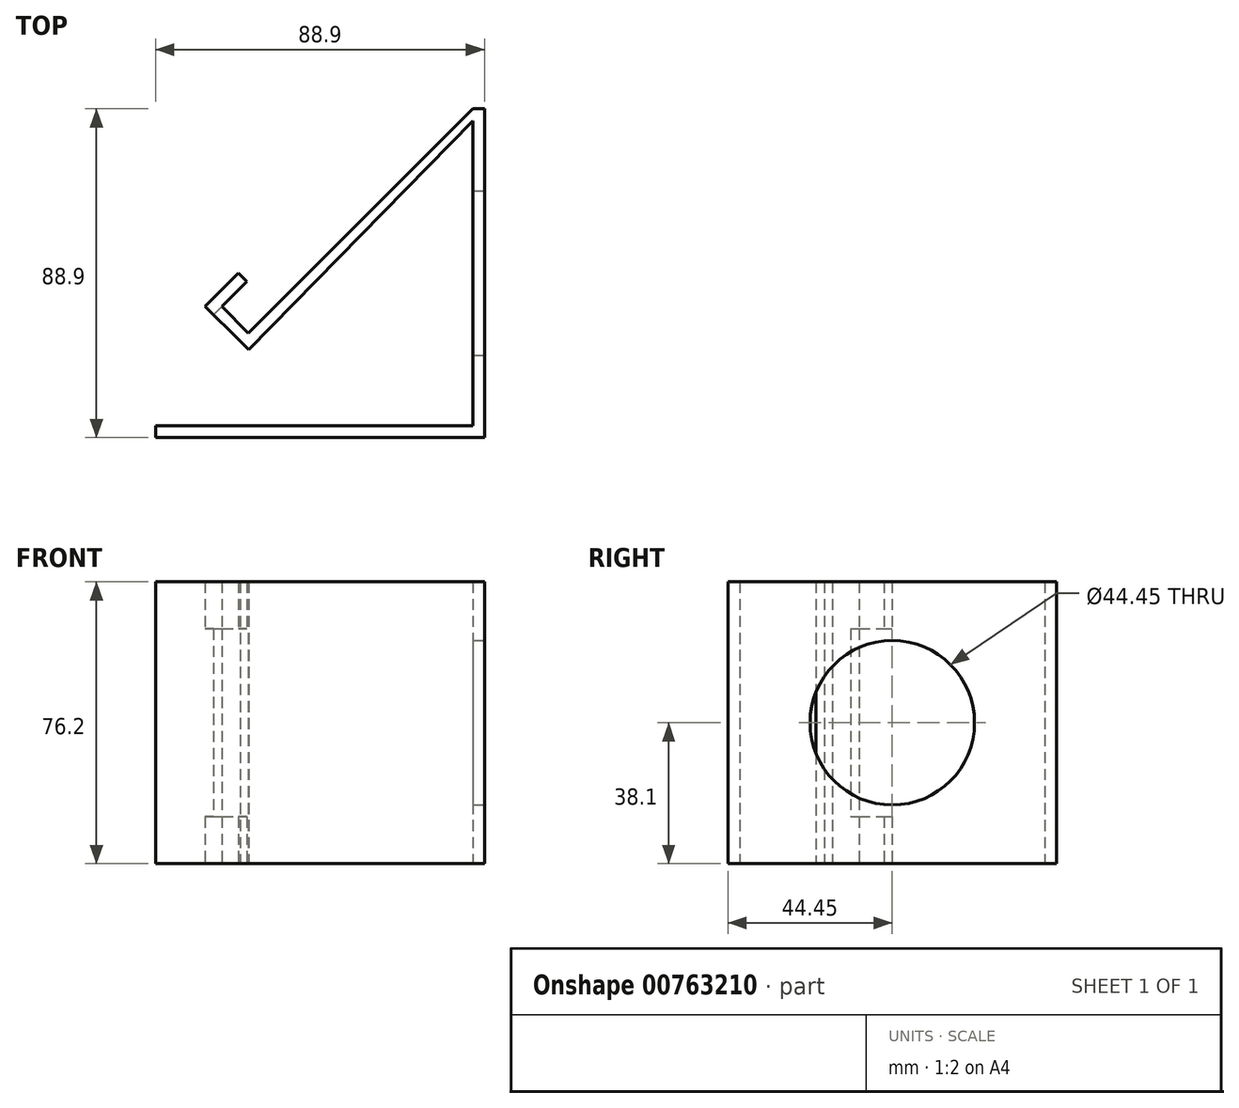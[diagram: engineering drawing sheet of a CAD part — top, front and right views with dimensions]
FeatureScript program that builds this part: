
annotation { "Feature Type Name" : "Feature", "Feature Type Description" : "" }
export const myFeature = defineFeature(function(context is Context, id is Id, definition is map)
    precondition{}
    {
        {
            var Q0;
            Q0=qCreatedBy(makeId("Top.planeOp"),FACE);
            var sketch = newSketch(context, id + "F0", { "sketchPlane" : qUnion([Q0])});
            skLineSegment(sketch, "E0.bottom", {"start": v(25.2, 38.37) * mm, "end": v(50.6, 38.37) * mm});
            skLineSegment(sketch, "E0.top", {"start": v(25.2, -8.48) * mm, "end": v(50.6, -8.48) * mm});
            skLineSegment(sketch, "E0.left", {"start": v(25.2, 38.37) * mm, "end": v(25.2, -8.48) * mm});
            skLineSegment(sketch, "E0.right", {"start": v(50.6, 38.37) * mm, "end": v(50.6, -8.48) * mm});
            skLineSegment(sketch, "E1", {"start": v(50.6, 38.37) * mm, "end": v(25.2, 65.41) * mm});
            skLineSegment(sketch, "E2", {"start": v(25.2, 65.41) * mm, "end": v(25.2, 38.37) * mm});
            skLineSegment(sketch, "E3", {"start": v(25.2, 65.41) * mm, "end": v(-24.23, -8.48) * mm});
            skLineSegment(sketch, "E4", {"start": v(-24.23, -8.48) * mm, "end": v(-19.15, -8.48) * mm});
            skLineSegment(sketch, "E5", {"start": v(-19.15, -8.48) * mm, "end": v(25.2, 59.38) * mm});
            skLineSegment(sketch, "E6", {"start": v(-19.79, -1.83) * mm, "end": v(-44.55, -1.83) * mm});
            skLineSegment(sketch, "E7", {"start": v(-44.55, -1.83) * mm, "end": v(-44.55, -8.48) * mm});
            skLineSegment(sketch, "E8", {"start": v(-44.55, -8.48) * mm, "end": v(-19.15, -8.48) * mm});
            skLineSegment(sketch, "E9", {"start": v(-44.55, -1.83) * mm, "end": v(-44.55, 5.8) * mm});
            skLineSegment(sketch, "E10", {"start": v(-44.55, 5.8) * mm, "end": v(-38.3, 5.8) * mm});
            skLineSegment(sketch, "E11", {"start": v(-38.3, 5.8) * mm, "end": v(-38.3, -1.83) * mm});
            skLineSegment(sketch, "E12", {"start": v(-44.55, -8.48) * mm, "end": v(-44.55, -21.18) * mm});
            skLineSegment(sketch, "E13", {"start": v(-44.55, -21.18) * mm, "end": v(-39.47, -21.18) * mm});
            skLineSegment(sketch, "E14", {"start": v(-39.47, -21.18) * mm, "end": v(-39.47, -8.48) * mm});
            skLineSegment(sketch, "E15", {"start": v(-24.23, -8.48) * mm, "end": v(-24.23, -21.18) * mm});
            skLineSegment(sketch, "E16", {"start": v(-24.23, -21.18) * mm, "end": v(-19.15, -21.18) * mm});
            skLineSegment(sketch, "E17", {"start": v(-19.15, -21.18) * mm, "end": v(-19.15, -8.48) * mm});
            skLineSegment(sketch, "E18", {"start": v(25.2, -8.48) * mm, "end": v(25.2, -21.18) * mm});
            skLineSegment(sketch, "E19", {"start": v(25.2, -21.18) * mm, "end": v(30.28, -21.18) * mm});
            skLineSegment(sketch, "E20", {"start": v(30.28, -21.18) * mm, "end": v(30.28, -8.48) * mm});
            skLineSegment(sketch, "E21", {"start": v(50.6, -21.18) * mm, "end": v(45.52, -21.18) * mm});
            skLineSegment(sketch, "E22", {"start": v(45.52, -21.18) * mm, "end": v(45.52, -8.48) * mm});
            skLineSegment(sketch, "E23", {"start": v(50.6, -21.18) * mm, "end": v(50.6, -8.48) * mm});
            skSolve(sketch);
        }
        {
            var Q0;
            Q0=qCreatedBy(makeId("Top.planeOp"),FACE);
            var sketch = newSketch(context, id + "F1", { "sketchPlane" : qUnion([Q0])});
            skLineSegment(sketch, "E24.bottom", {"start": v(-44.45, 0) * mm, "end": v(44.45, 0) * mm});
            skLineSegment(sketch, "E24.top", {"start": v(-44.45, 3.17) * mm, "end": v(44.45, 3.18) * mm});
            skLineSegment(sketch, "E24.left", {"start": v(-44.45, 0) * mm, "end": v(-44.45, 3.18) * mm});
            skLineSegment(sketch, "E24.right", {"start": v(44.45, 0) * mm, "end": v(44.45, 3.18) * mm});
            skPoint(sketch, "E25", {"position": v(0, 0) * mm});
            skLineSegment(sketch, "E26.bottom", {"start": v(44.45, 3.18) * mm, "end": v(41.28, 3.18) * mm});
            skLineSegment(sketch, "E26.top", {"start": v(44.45, 88.9) * mm, "end": v(41.27, 88.9) * mm});
            skLineSegment(sketch, "E26.left", {"start": v(44.45, 3.17) * mm, "end": v(44.45, 88.9) * mm});
            skLineSegment(sketch, "E26.right", {"start": v(41.28, 3.17) * mm, "end": v(41.28, 88.9) * mm});
            skLineSegment(sketch, "E27", {"start": v(44.45, 88.9) * mm, "end": v(-19.32, 23.82) * mm});
            skLineSegment(sketch, "E28", {"start": v(-19.32, 23.82) * mm, "end": v(-21.59, 26.04) * mm});
            skLineSegment(sketch, "E29", {"start": v(-21.59, 26.04) * mm, "end": v(41.27, 88.9) * mm});
            skLineSegment(sketch, "E30", {"start": v(-21.59, 26.04) * mm, "end": v(-31.02, 35.47) * mm});
            skLineSegment(sketch, "E31", {"start": v(-31.02, 35.47) * mm, "end": v(-22.04, 44.45) * mm});
            skLineSegment(sketch, "E32", {"start": v(-22.04, 44.45) * mm, "end": v(-19.8, 42.2) * mm});
            skLineSegment(sketch, "E33", {"start": v(-19.8, 42.2) * mm, "end": v(-26.53, 35.47) * mm});
            skLineSegment(sketch, "E34", {"start": v(-26.53, 35.47) * mm, "end": v(-19.34, 28.28) * mm});
            skSolve(sketch);
        }
        {
            var Q0;
            Q0=makeQuery(id+"F1.imprint","IMPRINT",FACE,{"disambiguationData":[TD([[makeQuery(id+"F1.imprint","IMPRINT",EDGE,{"derivedFrom":sQuery(id+"F1.wireOp",EDGE,"E24.bottom")}),1.0]])]});
            var Q1;
            {var subQ0=sQuery(id+"F1.wireOp",EDGE,"E26.left");Q1=makeQuery(id+"F1.imprint","IMPRINT",FACE,{"disambiguationData":[TD([[makeQuery(id+"F1.imprint","IMPRINT",EDGE,{"derivedFrom":subQ0}),1.0]])]});}
            var Q2;
            {var subQ4=sQuery(id+"F1.wireOp",EDGE,"E28");Q2=makeQuery(id+"F1.imprint","IMPRINT",FACE,{"disambiguationData":[TD([[makeQuery(id+"F1.imprint","IMPRINT",EDGE,{"derivedFrom":subQ4}),-1.0]])]});}
            var Q3;
            {var subQ0=sQuery(id+"F1.wireOp",EDGE,"E30");Q3=makeQuery(id+"F1.imprint","IMPRINT",FACE,{"disambiguationData":[TD([[makeQuery(id+"F1.imprint","IMPRINT",EDGE,{"derivedFrom":subQ0}),-1.0]])]});}
            var Q4;
            {var subQ0=sQuery(id+"F1.wireOp",EDGE,"E26.top");Q4=makeQuery(id+"F1.imprint","IMPRINT",FACE,{"disambiguationData":[TD([[makeQuery(id+"F1.imprint","IMPRINT",EDGE,{"derivedFrom":subQ0}),1.0]])]});}
            extrude(context, id + "F2", {"entities" : qUnion([Q0, Q1, Q2, Q3, Q4]), "depth" : 76.2 * mm, "offsetDistance" : 25.4 * mm});
        }
        {
            var Q0;
            Q0=makeQuery(id+"F2.opExtrude","SWEPT_FACE",FACE,{"disambiguationData":[OSD([sQuery(id+"F1.wireOp",EDGE,"E31")])]});
            var sketch = newSketch(context, id + "F3", { "sketchPlane" : qUnion([Q0])});
            skLineSegment(sketch, "E35.bottom", {"start": v(-3.15, 12.7) * mm, "end": v(-15.85, 12.7) * mm});
            skLineSegment(sketch, "E35.top", {"start": v(-3.15, 63.5) * mm, "end": v(-15.85, 63.5) * mm});
            skLineSegment(sketch, "E35.left", {"start": v(-3.15, 12.7) * mm, "end": v(-3.15, 63.5) * mm});
            skLineSegment(sketch, "E35.right", {"start": v(-15.85, 12.7) * mm, "end": v(-15.85, 63.5) * mm});
            skSolve(sketch);
        }
        {
            var Q0;
            Q0=makeQuery(id+"F3.imprint","IMPRINT",FACE,{"disambiguationData":[TD([[makeQuery(id+"F3.imprint","IMPRINT",EDGE,{"derivedFrom":sQuery(id+"F3.wireOp",EDGE,"E35.bottom")}),-1.0]])]});
            extrude(context, id + "F4", {"entities" : qUnion([Q0]), "operationType" : NewBodyOperationType.REMOVE, "oppositeDirection" : true, "depth" : 3.17 * mm, "offsetDistance" : 25.4 * mm});
        }
        {
            var Q0;
            Q0=makeQuery(id+"F2.opExtrude","SWEPT_FACE",FACE,{"disambiguationData":[OSD([sQuery(id+"F1.wireOp",EDGE,"E24.right"),sQuery(id+"F1.wireOp",EDGE,"E26.left")])]});
            var sketch = newSketch(context, id + "F5", { "sketchPlane" : qUnion([Q0])});
            skCircle(sketch, "E36", {"center": v(44.45, 38.1) * mm, "radius": 22.23 * mm});
            skLineSegment(sketch, "E37", {"start": v(88.9, 38.1) * mm, "end": v(0, 38.1) * mm, "construction": true});
            skLineSegment(sketch, "E38", {"start": v(44.45, 0) * mm, "end": v(44.45, 76.2) * mm});
            skSolve(sketch);
        }
        {
            var Q0;
            {var subQ0=sQuery(id+"F5.wireOp",EDGE,"E38");var subQ1=sQuery(id+"F5.wireOp",EDGE,"E36");var subQ2=makeQuery(id+"F5.imprint","INTERSECT",VERTEX,{"disambiguationData":[OD(0.0)],"derivedFrom":[subQ1,subQ0]});Q0=makeQuery(id+"F5.imprint","IMPRINT",FACE,{"disambiguationData":[TD([[makeQuery(id+"F5.imprint","IMPRINT",EDGE,{"disambiguationData":[TD([[subQ2,-1.0]])],"derivedFrom":subQ1}),1.0]])]});}
            var Q1;
            {var subQ0=sQuery(id+"F5.wireOp",EDGE,"E38");var subQ1=sQuery(id+"F5.wireOp",EDGE,"E36");var subQ2=makeQuery(id+"F5.imprint","INTERSECT",VERTEX,{"disambiguationData":[OD(0.0)],"derivedFrom":[subQ1,subQ0]});Q1=makeQuery(id+"F5.imprint","IMPRINT",FACE,{"disambiguationData":[TD([[makeQuery(id+"F5.imprint","IMPRINT",EDGE,{"disambiguationData":[TD([[subQ2,1.0]])],"derivedFrom":subQ1}),1.0]])]});}
            extrude(context, id + "F6", {"entities" : qUnion([Q0, Q1]), "operationType" : NewBodyOperationType.REMOVE, "oppositeDirection" : true, "depth" : 12.7 * mm, "offsetDistance" : 25.4 * mm});
        }
    });
